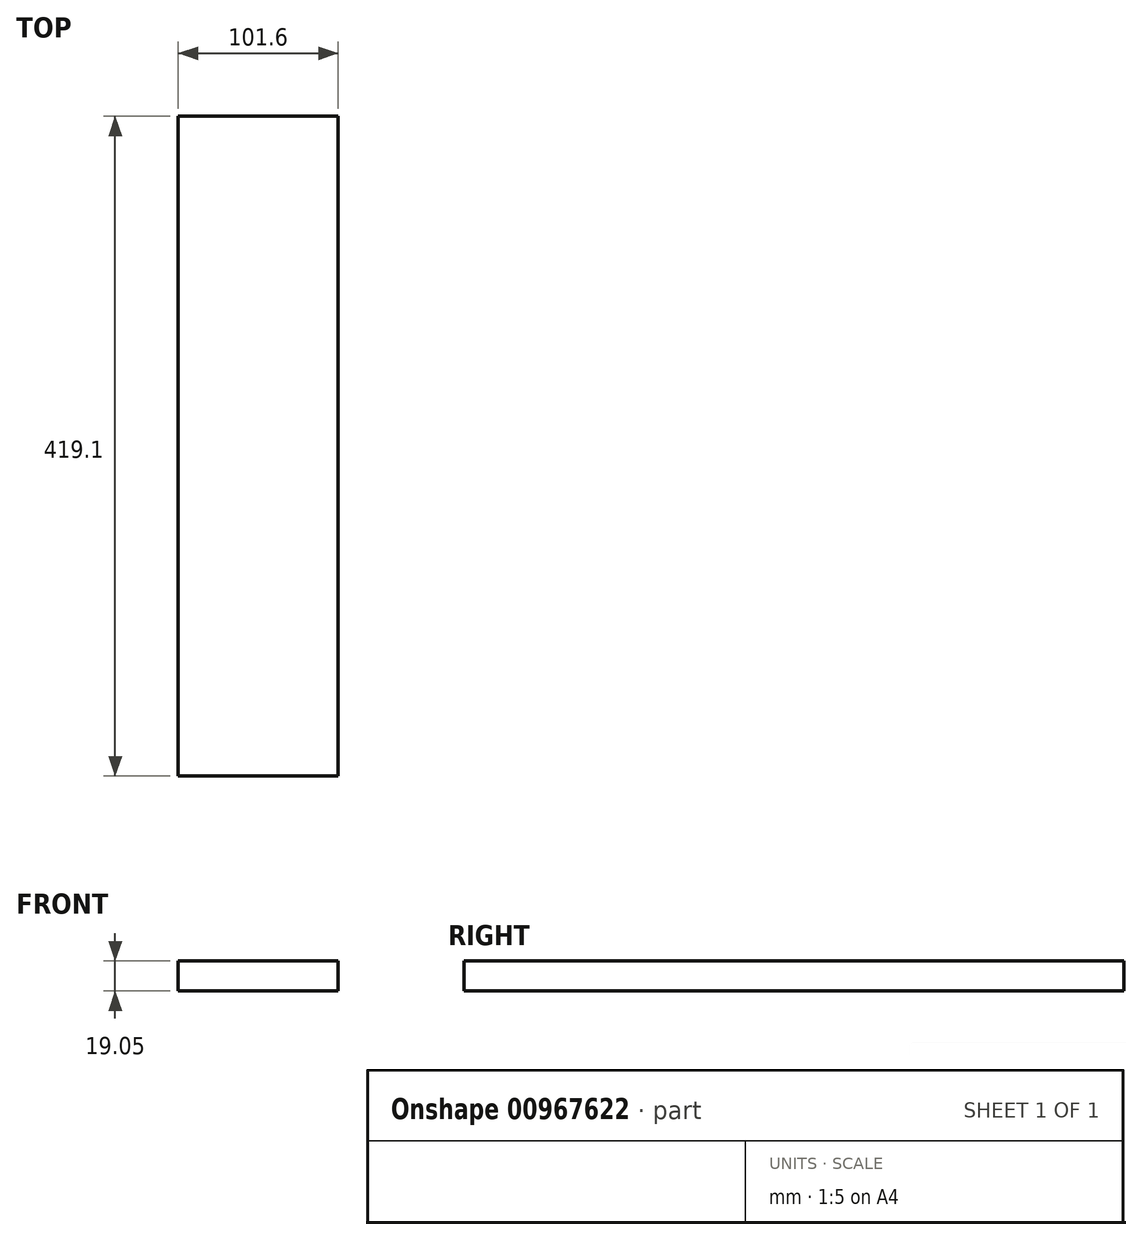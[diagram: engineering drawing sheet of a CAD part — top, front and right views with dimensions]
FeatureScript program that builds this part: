
annotation { "Feature Type Name" : "Feature", "Feature Type Description" : "" }
export const myFeature = defineFeature(function(context is Context, id is Id, definition is map)
    precondition{}
    {
        {
            var Q0;
            Q0=qCreatedBy(makeId("Top.planeOp"),FACE);
            var sketch = newSketch(context, id + "F0", { "sketchPlane" : qUnion([Q0])});
            skLineSegment(sketch, "E0.bottom", {"start": v(0, 0) * mm, "end": v(101.6, 0) * mm});
            skLineSegment(sketch, "E0.top", {"start": v(0, 419.1) * mm, "end": v(101.6, 419.1) * mm});
            skLineSegment(sketch, "E0.left", {"start": v(0, 0) * mm, "end": v(0, 419.1) * mm});
            skLineSegment(sketch, "E0.right", {"start": v(101.6, 0) * mm, "end": v(101.6, 419.1) * mm});
            skSolve(sketch);
        }
        {
            var Q0;
            Q0=makeQuery(id+"F0.imprint","IMPRINT",FACE,{"disambiguationData":[TD([[makeQuery(id+"F0.imprint","IMPRINT",EDGE,{"derivedFrom":sQuery(id+"F0.wireOp",EDGE,"E0.bottom")}),1.0]])]});
            extrude(context, id + "F1", {"entities" : qUnion([Q0]), "depth" : 19.05 * mm, "offsetDistance" : 25.4 * mm});
        }
    });
